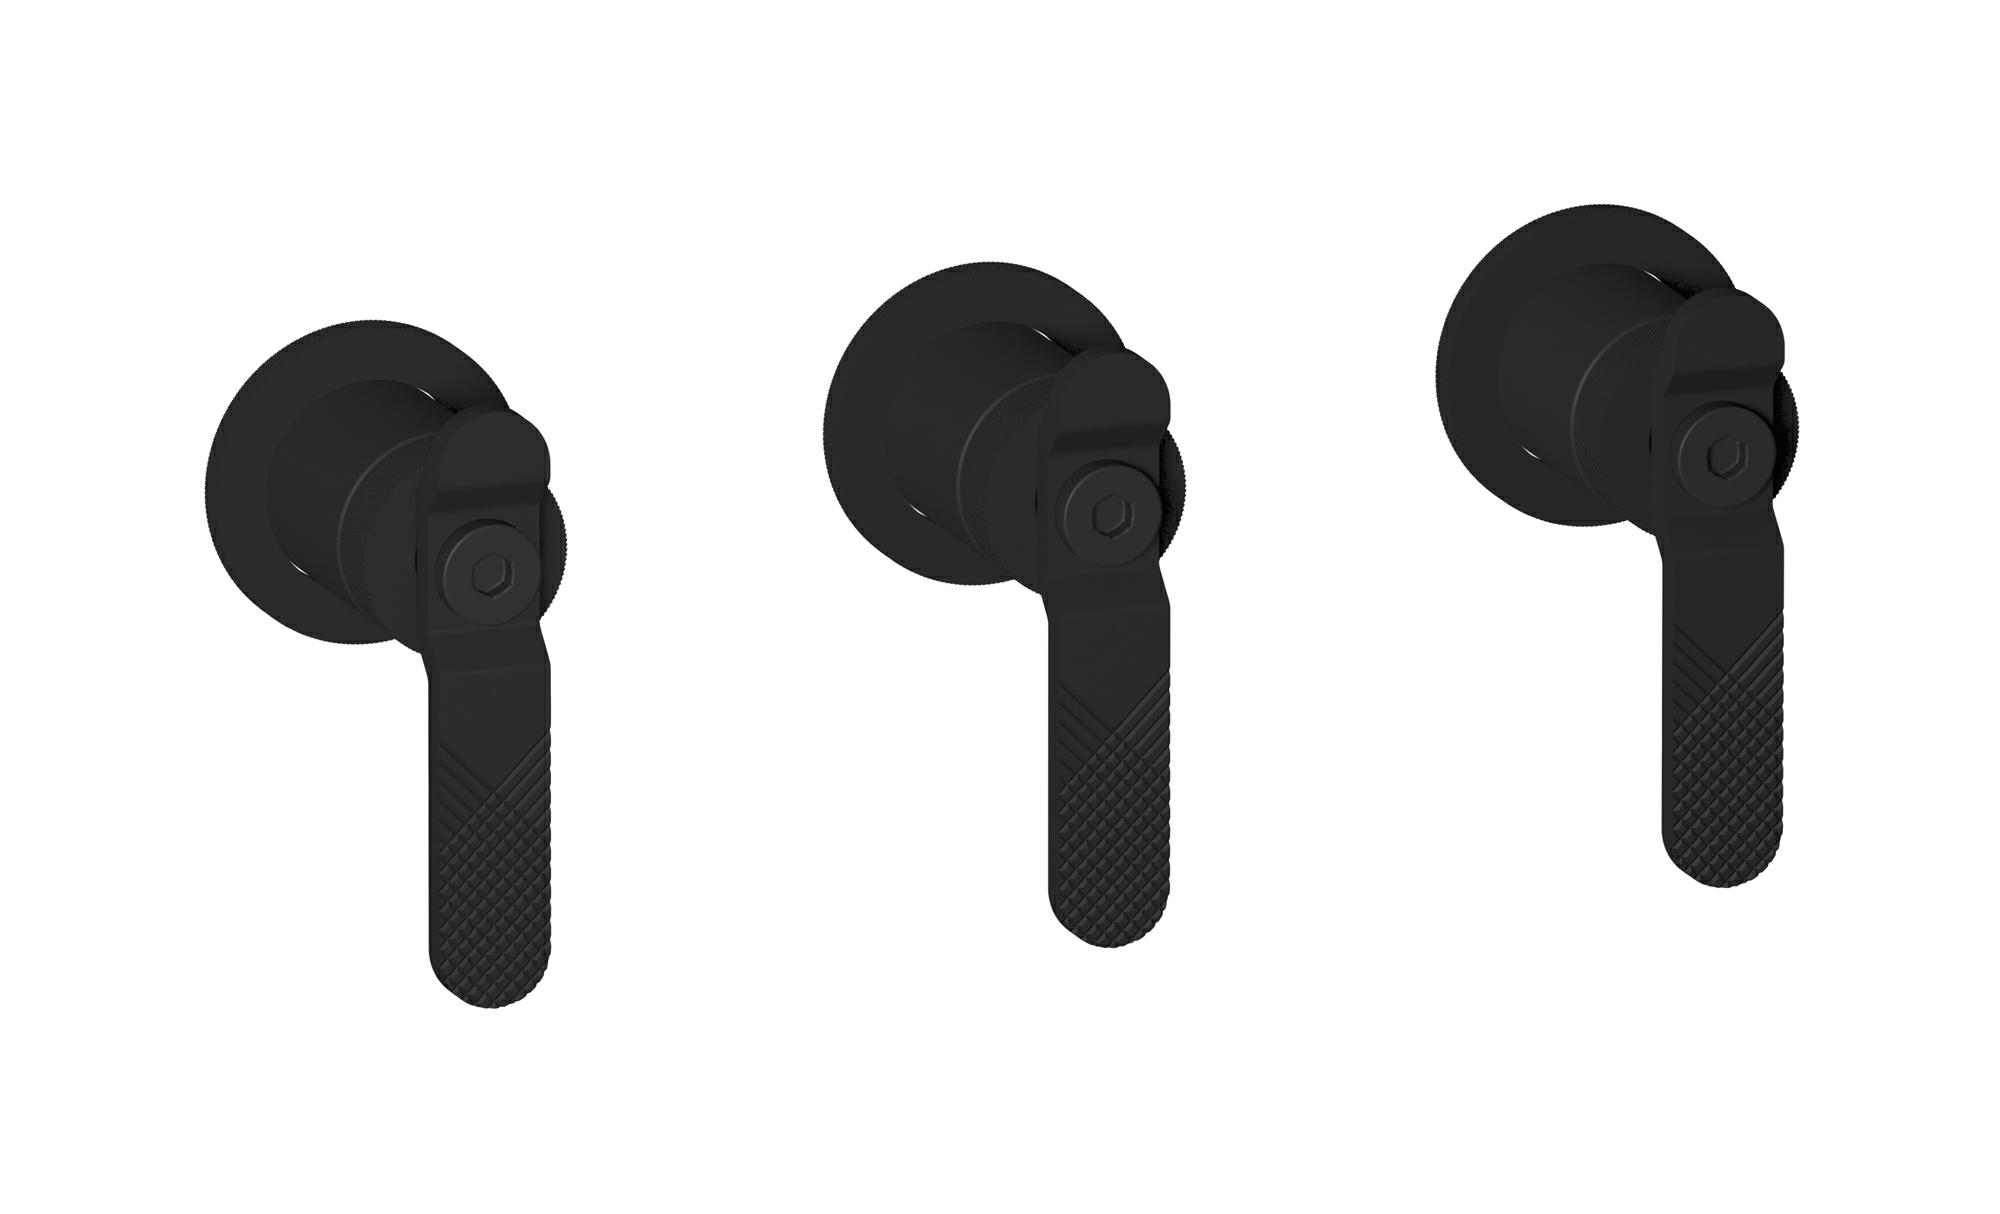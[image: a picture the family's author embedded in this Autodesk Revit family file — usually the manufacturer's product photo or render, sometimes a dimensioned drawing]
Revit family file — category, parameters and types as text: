
# Revit family: B2410
name_source: partatom
category: Apparecchi idraulici
units: mm (PartAtom-declared; Revit-internal decimal feet)

## family parameters
Basato su piano di lavoro = No
Condiviso = No
Mantieni orientamento annotazione = No
Numero OmniClass = 23.45.55.17
Punto di calcolo locali = No
Quota connettore circolare = Usa diametro
Sempre verticale = Sì
Taglio con vuoti quando caricato = No
Tipo di parte = Normale
Titolo OmniClass = Mixing Faucets

## types (13) — shared parameters
Cold water inlet = 10 mm  [stored 0.0328084 ft]
Commenti sul tipo = Three holes wall mounted shower with two ways diverter
Connessione CW = No
Connessione HW = No
Connessione di scarico = No
Connessione di ventilazione = No
Descrizione = Three holes wall mounted shower with two ways diverter
Hot water inlet = 10 mm  [stored 0.0328084 ft]
Produttore = IB Rubinetterie S.p.A.
URL = https://www.weareib.it
zero-valued in all types: Prospetto di default

## per-type parameters (varying)
| type | Finishes surface | Immagine tipo | Modello |
| Chrome | IB_Chrome | B2410CC.jpg | B2410CC |
| Black Chrome | IB_Black chrome | B2410CF.jpg | B2410CF |
| Brushed Black Chrome | IB_Brushed black chrome | B2410CS.jpg | B2410CS |
| Pale Gold | IB_Pale gold | B2410II.jpg | B2410II |
| Brushed Pale Gold | IB_brushed pale gold | B2410IS.jpg | B2410IS |
| Modern Bronze | IB_Modern bronze | B2410MB.jpg | B2410MB |
| Matt Black | IB_matt black | B2410NP.jpg | B2410NP |
| Natural Brass | IB_Brass | B2410ON.jpg | B2410ON |
| Gold | IB_gold | B2410OO.jpg | B2410OO |
| Brushed Gold | IB_brushed gold | B2410OS.jpg | B2410OS |
| Rose Gold | IB_Rose gold | B2410RS.jpg | B2410RS |
| Brushed Rose Gold | IB_Brushed rose gold | B2410SR.jpg | B2410SR |
| Brushed Nickel | IB_Brushed nickel | B2410SS.jpg | B2410SS |

note: [stored X ft] marks values corroborated as IEEE doubles in the binary element streams (Revit-internal decimal feet)
